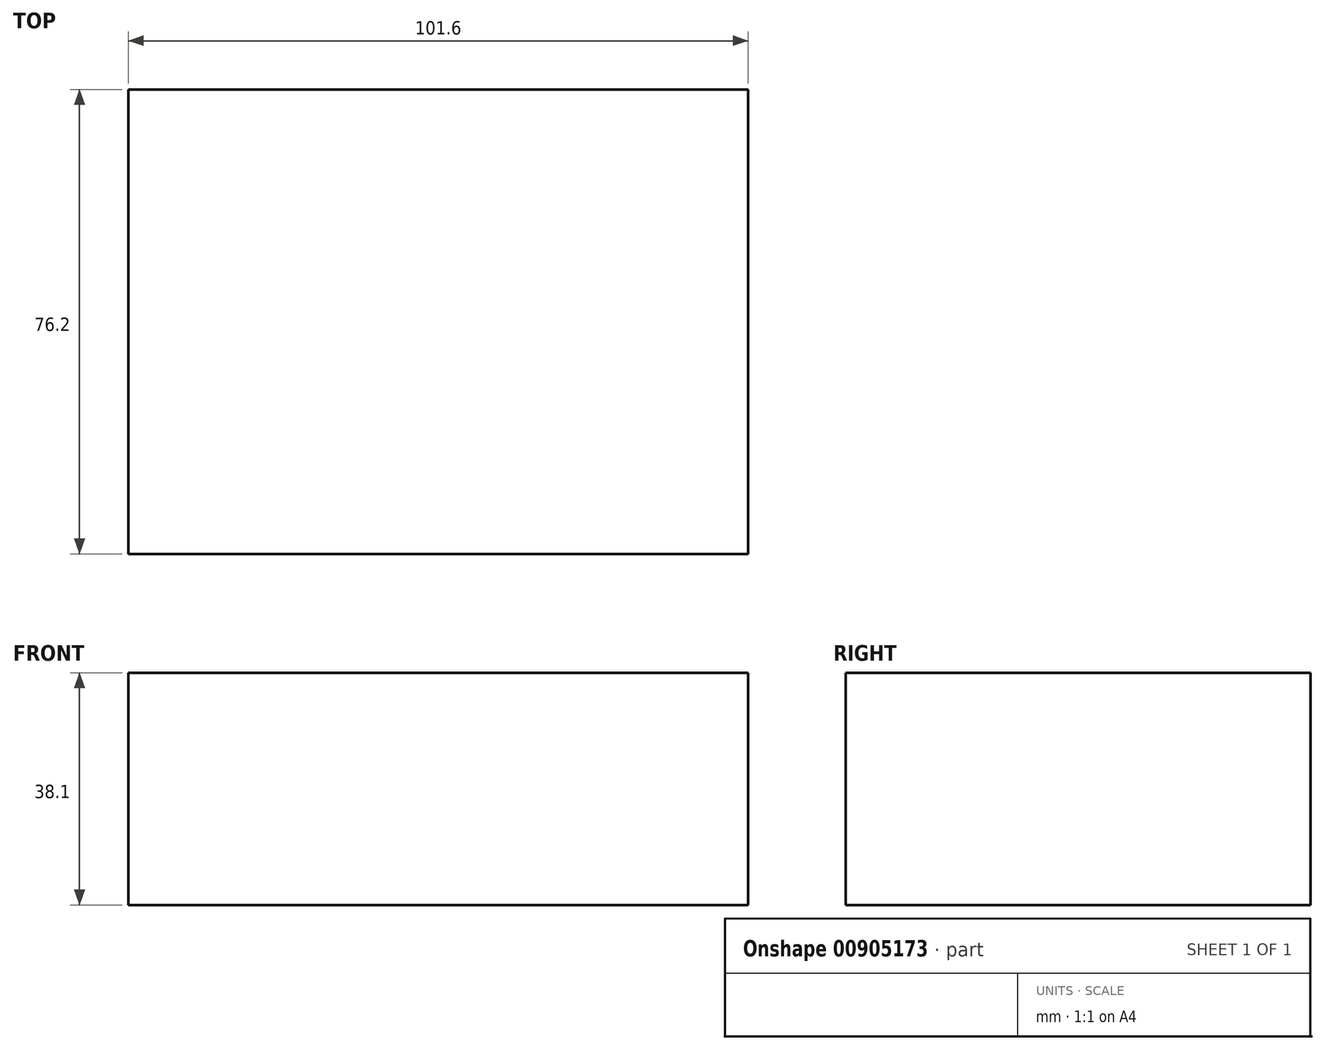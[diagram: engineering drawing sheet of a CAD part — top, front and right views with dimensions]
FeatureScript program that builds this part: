
annotation { "Feature Type Name" : "Feature", "Feature Type Description" : "" }
export const myFeature = defineFeature(function(context is Context, id is Id, definition is map)
    precondition{}
    {
        {
            var Q0;
            Q0=qCreatedBy(makeId("Top.planeOp"),FACE);
            var sketch = newSketch(context, id + "F0", { "sketchPlane" : qUnion([Q0])});
            skLineSegment(sketch, "E0.bottom", {"start": v(50.8, 38.1) * mm, "end": v(-50.8, 38.1) * mm});
            skLineSegment(sketch, "E0.top", {"start": v(50.8, -38.1) * mm, "end": v(-50.8, -38.1) * mm});
            skLineSegment(sketch, "E0.left", {"start": v(50.8, 38.1) * mm, "end": v(50.8, -38.1) * mm});
            skLineSegment(sketch, "E0.right", {"start": v(-50.8, 38.1) * mm, "end": v(-50.8, -38.1) * mm});
            skPoint(sketch, "E0.middle", {"position": v(0, 0) * mm});
            skPoint(sketch, "E1.visualSharp", {"position": v(-50.8, 38.1) * mm});
            skPoint(sketch, "E2.visualSharp", {"position": v(50.8, 38.1) * mm});
            skPoint(sketch, "E3.visualSharp", {"position": v(50.8, -38.1) * mm});
            skPoint(sketch, "E4.visualSharp", {"position": v(-50.8, -38.1) * mm});
            skSolve(sketch);
        }
        {
            var Q0;
            Q0 = qSketchRegion(id + "F0", true);
            extrude(context, id + "F1", {"entities" : qUnion([Q0]), "depth" : 38.1 * mm, "offsetDistance" : 25.4 * mm});
        }
        {
            var Q0;
            Q0=makeQuery(id+"F1.opExtrude","SWEPT_FACE",FACE,{"disambiguationData":[OSD([sQuery(id+"F0.wireOp",EDGE,"E0.left")])]});
            cPlane(context, id + "F2", {"entities" : qUnion([Q0]), "cplaneType" : CPlaneType.OFFSET, "offset" : 6.35 * mm, "oppositeDirection" : true, "width" : 152.4 * mm, "height" : 152.4 * mm});
        }
    });
